# Revit family: Gira_215004
name_source: partatom
category: Elektroinstallationen
revit_build: Autodesk Revit 2017 (Build: 20160225_1515(x64)
units: mm (PartAtom-declared; Revit-internal decimal feet)

## family parameters
Basisbauteil = Fläche
Beim Laden mit Abzugskörper schneiden = Nein
Bemaßung runder Anschluss = Durchmesser verwenden
Beschriftungsausrichtung beibehalten = Nein
Gemeinsam genutzt = Nein
Raumberechnungspunkt = Nein
Teiletyp = Normal

## types (1)
- Gira_215004
    Acoustic signal = Nein
    Analogue input = Nein
    BIM = https://media.stage.bim.site
    Beschreibung = Weather st.Std KNX,KNX weather station Standard,,,Features:,- Weather station Standard for measuring and evaluating weather data (wind speed, precipitation, twilight, temperature, and brightness).,- Installation outdoors of buildings, preferably in the roof area.,- Temperature sensor for measuring the outdoor temperature.,- Wind sensor (thermal) for determining the wind speed.,- Twilight sensor for measuring the brightness in the twilight range.,- Three brightness sensors offset by 90 determine the brightness in daylight and sunshine, direction-dependent.,- Rain sensor for recording precipitation.,- A teach-in function enables the application of a current measured value as a limit. This can, for example, be triggered by pressing an external button.,- Two limits with an adjustable hysteresis per sensor (except rain sensor) can be parameterised.,- All limit objects have a parameterisable switch-on and switch-off delay.,- Six logic gates (AND, AND with return, OR, Exclusive OR, NAND, NOR) with up to four inputs for external and internal 1 bit values.,- Four blocking elements for blocking functions or manual operation.,- Cyclical transmission in case of a value change.,,Notes :,- Direct sunlight can impact temperature measurement.
    Bus connection included = Nein
    Bus system KNX = Ja
    Bus system KNX radio = Nein
    Bus system LON = Nein
    Bus system Powernet = Nein
    Bus system radio frequent = Nein
    Colour = Aluminium
    Data sheet = https://katalog.gira.de
    Degree of protection (IP) = IP44
    GTIN = 4010337058441
    HAN = 215004
    Hersteller = Gira
    Model = Other
    Mounting method = Surface mounted (plaster)
    Other bus systems = Other
    Productwebsite = http://katalog.gira.de
    Typname = Weather st. Standard KNX
    URL = https://www.gira.de
    Vorgabe-Ansicht = 1219 mm
    Weather station = Nein
    With DCF77 = Nein
    With heating = Nein

## geometry (parser evidence)
native form markers: Sweep x1
no freeform markers — native parametric forms only
